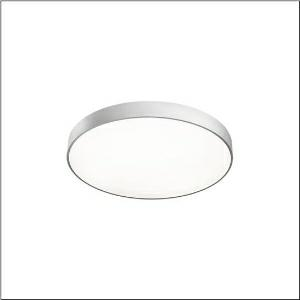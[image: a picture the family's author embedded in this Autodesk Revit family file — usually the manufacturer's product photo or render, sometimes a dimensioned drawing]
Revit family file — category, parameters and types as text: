
# Revit family: round_21_m_51mr36fm8421s
name_source: partatom
category: Lighting Fixtures
units: mm (PartAtom-declared; Revit-internal decimal feet)

## family parameters
Cut with Voids When Loaded = No
Host = Face
Light Source = No
Part Type = Normal
Room Calculation Point = No
Round Connector Dimension = Use Diameter
Shared = No

## types (1)
- --- (1 x LED, 8900 lm, 62.6 W, 4000K)
    Apparent Load = 63 VA
    CIE Flux Codes = 49 80 96 100 100
    Color Rendering = 80
    Color Temperature = 4000K
    Default Elevation = 1800 mm
    Description = Round 21 M, wall and ceiling luminaire, primary optical cover: cover, of PMMA, opal, light emission: direct distribution, primary light characteristic: symmetric, installation type: suspended mounting, surface-mounted, LED, rated luminous flux: 8.140lm, luminous efficacy: 133lm/W, light colour: 840, colour temperature: 4000K, control gear: ON/OFF Multilumen, with terminal, 3-pole, mains connection: 230V, AC, 50/60Hz, rated input power: 61W, housing, of aluminium, coated, silver, diameter: 600mm, height: 62mm, protection rating (complete): IP40, insulation class (complete): insulation class I (protective earthing), certification: CE, impact resistance: IK04, permissible operating ambient temperature: -10..+35°C, packaging unit: 1 piece
    Height = 87 mm
    Lamp = 1 x LED
    Lamp Light Flux = 8900 lm
    Lamp Power = 62.6 W
    Lamp count = 1
    Length = 600 mm
    Luminous efficacy = 142 lm/W
    Manufacturer = Siteco
    ModVariant = No
    Model = 51MR36FM8421S
    Mounting Place = Ceiling
    Mounting Type = Surface mounted
    Number of Poles = 1
    OnlyDefault = Yes
    Power Factor = 1
    Product Name = Round 21 M
    Product group = wall and ceiling luminaire | ceiling mounted
    ProductGroupID = 304
    Protection Class = Protection class I
    Protection Degree = IP 40
    RLX_Detail_Level = 1
    RLX_Emergency_Light_Flux = 0 lm
    RLX_Emergency_Type = 0
    RLX_Emergency_Type_DB = No
    RlxData = <blob elided: 17525 chars, md5=64b9387f>
    Socket = socket
    Standby Power = 0 W
    System Light Flux = 8900 lm
    System Power = 63 W
    Type Comments = factory setting: luminous flux: 100 % | (ON | ON | ON | ON) | 700 mA
    Type Image = l_1258303.jpg
    URL = http://relux.com
    VarID = @adj_039449
    Voltage = 0 V
    Weight = 0.00 kg
    Width = 0 mm  [stored 0 ft]

note: [stored X ft] marks values corroborated as IEEE doubles in the binary element streams (Revit-internal decimal feet)

## geometry (parser evidence)
native form markers: Blend x4, Sweep x11
no freeform markers — native parametric forms only
